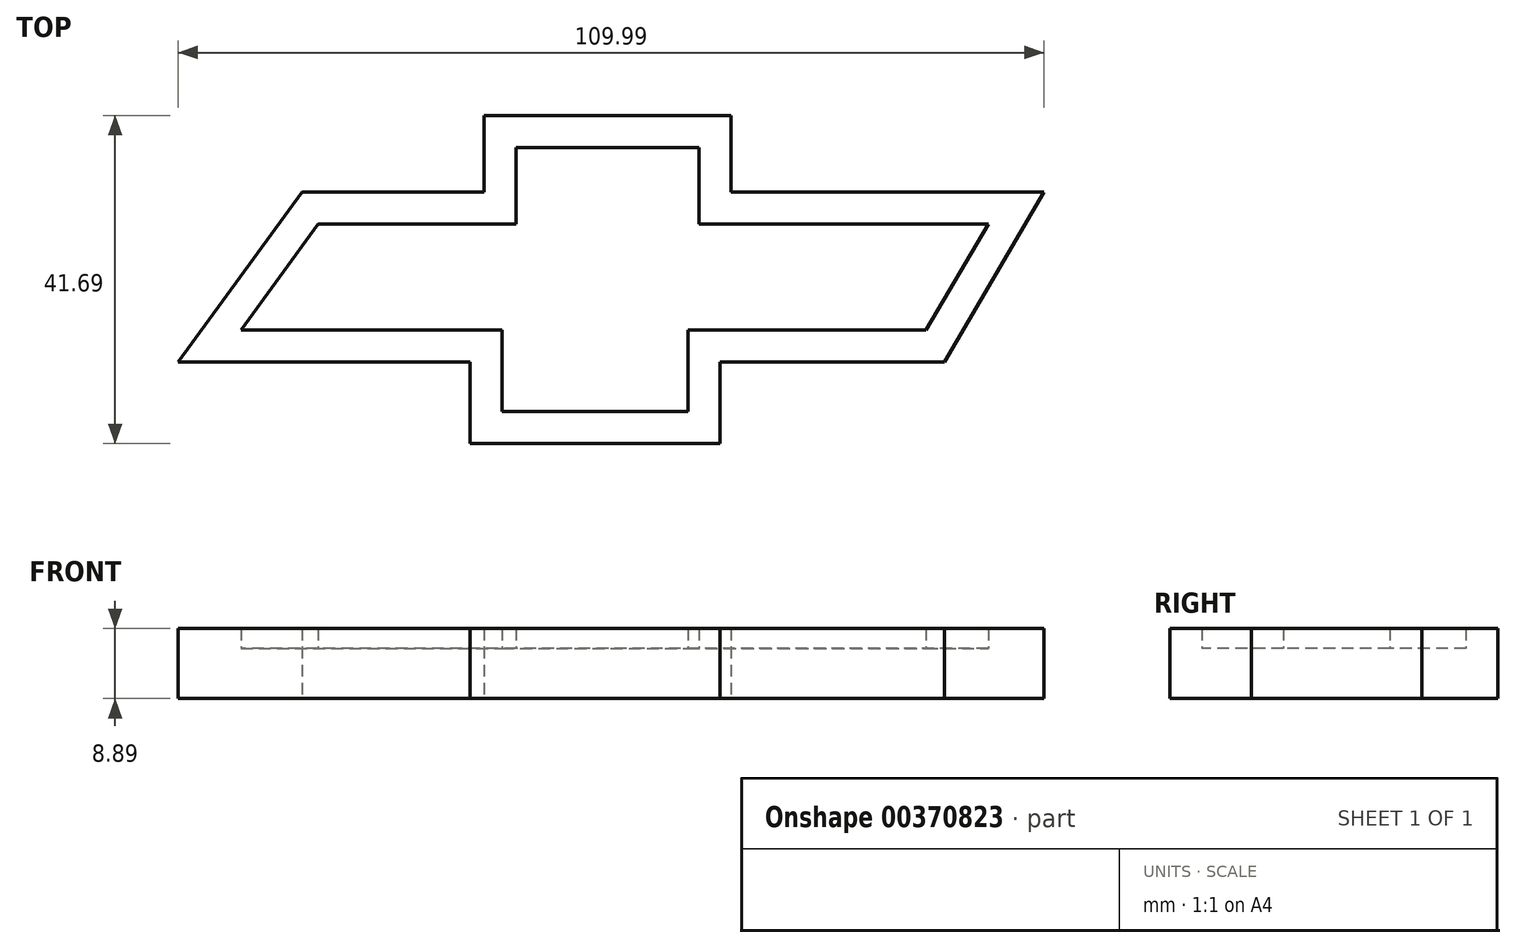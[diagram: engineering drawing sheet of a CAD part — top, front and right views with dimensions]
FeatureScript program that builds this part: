
annotation { "Feature Type Name" : "Feature", "Feature Type Description" : "" }
export const myFeature = defineFeature(function(context is Context, id is Id, definition is map)
    precondition{}
    {
        {
            var Q0;
            Q0=qCreatedBy(makeId("Top.planeOp"),FACE);
            var sketch = newSketch(context, id + "F0", { "sketchPlane" : qUnion([Q0])});
            skLineSegment(sketch, "E0", {"start": v(-42.23, 7.36) * mm, "end": v(-57.95, -14.27) * mm});
            skLineSegment(sketch, "E1", {"start": v(-57.95, -14.27) * mm, "end": v(-20.85, -14.27) * mm});
            skLineSegment(sketch, "E2", {"start": v(-20.85, -14.27) * mm, "end": v(-20.85, -24.62) * mm});
            skLineSegment(sketch, "E3", {"start": v(-20.85, -24.62) * mm, "end": v(10.87, -24.62) * mm});
            skLineSegment(sketch, "E4", {"start": v(10.87, -24.62) * mm, "end": v(10.87, -14.27) * mm});
            skLineSegment(sketch, "E5", {"start": v(-42.23, 7.36) * mm, "end": v(-19.07, 7.36) * mm});
            skLineSegment(sketch, "E6", {"start": v(-19.07, 7.36) * mm, "end": v(-19.07, 17.07) * mm});
            skLineSegment(sketch, "E7", {"start": v(-19.07, 17.07) * mm, "end": v(12.26, 17.07) * mm});
            skLineSegment(sketch, "E8", {"start": v(12.26, 17.07) * mm, "end": v(12.26, 7.36) * mm});
            skLineSegment(sketch, "E9", {"start": v(10.87, -14.27) * mm, "end": v(39.4, -14.27) * mm});
            skLineSegment(sketch, "E10", {"start": v(12.26, 7.36) * mm, "end": v(52.04, 7.36) * mm});
            skLineSegment(sketch, "E11", {"start": v(52.04, 7.36) * mm, "end": v(39.4, -14.27) * mm});
            skSolve(sketch);
        }
        {
            var Q0;
            Q0=makeQuery(id+"F0.imprint","IMPRINT",FACE,{"disambiguationData":[TD([[makeQuery(id+"F0.imprint","IMPRINT",EDGE,{"derivedFrom":sQuery(id+"F0.wireOp",EDGE,"E0")}),1.0]])]});
            extrude(context, id + "F1", {"entities" : qUnion([Q0]), "depth" : 6.35 * mm});
        }
        {
            var Q0;
            Q0=makeQuery(id+"F1.opExtrude","CAP_FACE",FACE,{"disambiguationData":[OSD([sQuery(id+"F0.wireOp",EDGE,"E0"),sQuery(id+"F0.wireOp",EDGE,"E1"),sQuery(id+"F0.wireOp",EDGE,"E2"),sQuery(id+"F0.wireOp",EDGE,"E3"),sQuery(id+"F0.wireOp",EDGE,"E4"),sQuery(id+"F0.wireOp",EDGE,"E5"),sQuery(id+"F0.wireOp",EDGE,"E6"),sQuery(id+"F0.wireOp",EDGE,"E7"),sQuery(id+"F0.wireOp",EDGE,"E8"),sQuery(id+"F0.wireOp",EDGE,"E9"),sQuery(id+"F0.wireOp",EDGE,"E10"),sQuery(id+"F0.wireOp",EDGE,"E11")])],"isStart":false});
            var sketch = newSketch(context, id + "F2", { "sketchPlane" : qUnion([Q0])});
            skLineSegment(sketch, "E12", {"start": v(-42.23, 7.36) * mm, "end": v(-57.95, -14.27) * mm});
            skLineSegment(sketch, "E13", {"start": v(-57.95, -14.27) * mm, "end": v(-20.85, -14.27) * mm});
            skLineSegment(sketch, "E14", {"start": v(-20.85, -14.27) * mm, "end": v(-20.85, -24.62) * mm});
            skLineSegment(sketch, "E15", {"start": v(-20.85, -24.62) * mm, "end": v(10.87, -24.62) * mm});
            skLineSegment(sketch, "E16", {"start": v(10.87, -24.62) * mm, "end": v(10.87, -14.27) * mm});
            skLineSegment(sketch, "E17", {"start": v(10.87, -14.27) * mm, "end": v(39.4, -14.27) * mm});
            skLineSegment(sketch, "E18", {"start": v(39.4, -14.27) * mm, "end": v(52.04, 7.36) * mm});
            skLineSegment(sketch, "E19", {"start": v(52.04, 7.36) * mm, "end": v(12.26, 7.36) * mm});
            skLineSegment(sketch, "E20", {"start": v(12.26, 7.36) * mm, "end": v(12.26, 17.07) * mm});
            skLineSegment(sketch, "E21", {"start": v(12.26, 17.07) * mm, "end": v(-19.07, 17.07) * mm});
            skLineSegment(sketch, "E22", {"start": v(-19.07, 17.07) * mm, "end": v(-19.07, 7.36) * mm});
            skLineSegment(sketch, "E23", {"start": v(-19.07, 7.36) * mm, "end": v(-42.23, 7.36) * mm});
            skLineSegment(sketch, "E24.0", {"start": v(-15, 13) * mm, "end": v(-15, 3.3) * mm});
            skLineSegment(sketch, "E24.1", {"start": v(-16.79, -20.55) * mm, "end": v(6.8, -20.55) * mm});
            skLineSegment(sketch, "E24.2", {"start": v(-16.79, -10.2) * mm, "end": v(-16.79, -20.55) * mm});
            skLineSegment(sketch, "E24.3", {"start": v(-49.97, -10.2) * mm, "end": v(-16.79, -10.2) * mm});
            skLineSegment(sketch, "E24.4", {"start": v(-40.16, 3.3) * mm, "end": v(-49.97, -10.2) * mm});
            skLineSegment(sketch, "E24.5", {"start": v(6.8, -20.55) * mm, "end": v(6.8, -10.2) * mm});
            skLineSegment(sketch, "E24.6", {"start": v(-15, 3.3) * mm, "end": v(-40.16, 3.3) * mm});
            skLineSegment(sketch, "E24.7", {"start": v(6.8, -10.2) * mm, "end": v(37.07, -10.2) * mm});
            skLineSegment(sketch, "E24.8", {"start": v(37.07, -10.2) * mm, "end": v(44.96, 3.3) * mm});
            skLineSegment(sketch, "E24.9", {"start": v(44.96, 3.3) * mm, "end": v(8.2, 3.3) * mm});
            skLineSegment(sketch, "E24.10", {"start": v(8.2, 3.3) * mm, "end": v(8.2, 13) * mm});
            skLineSegment(sketch, "E24.11", {"start": v(8.2, 13) * mm, "end": v(-15, 13) * mm});
            skSolve(sketch);
        }
        {
            var Q0;
            Q0 = qSketchRegion(id + "F2", true);
            extrude(context, id + "F3", {"entities" : qUnion([Q0]), "operationType" : NewBodyOperationType.ADD, "depth" : 2.54 * mm});
        }
    });
